# Revit family: PRD_FrankeWS_DspslChts_DisposalChute_RODX607TT
name_source: partatom
category: Plumbing Fixtures
revit_build: Autodesk Revit 2018 (Build: 20190510_1515(x64)
units: mm (PartAtom-declared; Revit-internal decimal feet)

## family parameters
Cut with Voids When Loaded = No
Host = Face
OmniClass Number = 23.45.30.00
OmniClass Title = Washing and Waste Disposal Equipment
Part Type = Normal
Room Calculation Point = No
Round Connector Dimension = Use Diameter
Shared = No

## types (1)
- RODX607TT
    AssetType = Fixed
    BIMObjectName = PRD_AR_DspslChts_DisposalChute_RODX607TT
    Category = Pr_65_12_70_22, Disposal chutes
    Color = stainless steel
    Default Elevation = 0 mm  [stored 0 ft]
    Description = Waste chute for table top installation, stainless steel, visible surfaces satin finished, material thickness 0.8 mm, without waste container.
Dimensions 175 x 121 x 175 mm (W x H x D)
    DurationUnit = year
    Features = stainless steel, 0.8 mm, satin finished, table top installation, 175x121x175 mm (WxHxD)
    Finish = satin finished
    FinishAndMaterial = stainless steel
    Form = waste chute for table top installation
    GrossWeight = 0.88 kg
    IfcExportAs = IfcSanitaryTerminalType
    IfcExportType = COMMON
    Manufacturer = KWC Group AG
    ManufacturerName = KWC Group AG
    ManufacturerURL = www.kwc.com
    Material = stainless steel
    MaterialsBody = Stainless steel 1.4301
    MaterialsFinishAndColour = Satin finished
    Model = RODX607TT
    ModelNumber = 2000101212
    ModelReference = RODX607TT
    NBSDescription = Disposal chutes
    NBSReference = 45-30-15/310
    Name = Waste chute RODX607TT
    NetWeight = 0.75 kg
    NominalDepth = 175 mm  [stored 0.574147 ft]
    NominalHeight = 121 mm  [stored 0.396982 ft]
    NominalWidth = 175 mm  [stored 0.574147 ft]
    ProductInformation = https://pim.kwc.com
    Shape = Rectangular
    Size = 175 x 121 x 175 mm
    TypeOfFixing = Screw glue
    TypeOfMounting = Counter top mounting
    URL = www.kwc.com
    Uniclass2015Code = Pr_65_12_70_22
    Uniclass2015Title = Disposal chutes
    Uniclass2015Version = Products v1.7
    Version = 1
    WarrantyDurationUnit = year
    WashbasinMaterial = PRD_AR_StainlessSteel_SatinFinished

note: [stored X ft] marks values corroborated as IEEE doubles in the binary element streams (Revit-internal decimal feet)

## geometry (parser evidence)
native form markers: Sweep x4
no freeform markers — native parametric forms only
